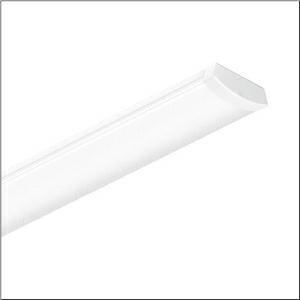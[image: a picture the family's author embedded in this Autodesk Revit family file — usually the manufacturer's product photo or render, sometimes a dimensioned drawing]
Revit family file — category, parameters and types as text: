
# Revit family: siluette_r__21_51ln12mnm70a3g_252a
name_source: partatom
category: Lighting Fixtures
units: mm (PartAtom-declared; Revit-internal decimal feet)

## family parameters
Cut with Voids When Loaded = No
Host = Face
Light Source = No
Part Type = Normal
Room Calculation Point = No
Round Connector Dimension = Use Diameter
Shared = No

## types (1)
- --- (1 x LED, 4320 lm, 28.8 W, 5000K)
    Apparent Load = 29 VA
    CIE Flux Codes = 43 73 92 94 100
    Color Rendering = 80
    Color Temperature = 5000K
    Default Elevation = 1800 mm
    Description = Siluette® 21, office luminaire, primary optical cover: enclosure, of PC, frosted, light emission: direct distribution, primary light characteristic: symmetric, installation type: suspended mounting, surface-mounted, LED, rated luminous flux: 7.150lm, luminous efficacy: 142lm/W, light colour: 830/840/850, colour temperature: 3000/4000/5000K, control gear: ON/OFF Multilumen, with terminal, 4-pole, mains connection: 220..240V, AC, 50/60Hz, rated input power: 51W, control gear: single battery element, housing, of sheet steel, white, length: 1.500mm, width: 152mm, height: 53mm, end cap, of PMMA, white, protection rating (complete): IP44, insulation class (complete): insulation class I (protective earthing), certification: CE, UKCA, protection symbol: D, impact resistance: IK04, permissible operating ambient temperature: +5..+40°C, standard: EN 60598-2-22, corresponds to IFS (International Featured Standards) requirements for safety and quality in the food industry, contact your sales advisor before using the luminaires in applications with unclear chemical exposure, large temperature fluctuations or condensation-forming humidity, packaging unit: 1 piece
    Height = 52 mm  [stored 0.170604 ft]
    Lamp = 1 x LED
    Lamp Light Flux = 4320 lm
    Lamp Power = 28.8 W
    Lamp count = 1
    Length = 1485 mm
    Luminous efficacy = 150 lm/W
    Manufacturer = Siteco
    ModVariant = No
    Model = 51LN12MNM70A3G
    Mounting Place = Ceiling
    Mounting Type = Pendant
    Number of Poles = 1
    OnlyDefault = Yes
    Power Factor = 1
    Product Name = Siluette® 21
    Product group = office luminaire | ceiling pendant
    ProductGroupID = 904
    Protection Class = Protection class I
    Protection Degree = IP 44
    RLX_Detail_Level = 1
    RLX_Emergency_Light_Flux = 0 lm
    RLX_Emergency_Type = 0
    RLX_Emergency_Type_DB = No
    RlxData = <blob elided: 19533 chars, md5=ca0e0d78>
    Socket = socket
    Standby Power = 0 W
    System Light Flux = 4320 lm
    System Power = 29 W
    Type Comments = individual setting: colour temperature 5000K, luminous flux: 61 % | (OFF | OFF | ON) | 200 mA
    Type Image = l_1296910.jpg
    URL = http://relux.com
    VarID = @adj_059350
    Voltage = 0 V
    Weight = 0.00 kg
    Width = 152 mm

note: [stored X ft] marks values corroborated as IEEE doubles in the binary element streams (Revit-internal decimal feet)

## geometry (parser evidence)
native form markers: Blend x4, Sweep x11
no freeform markers — native parametric forms only
